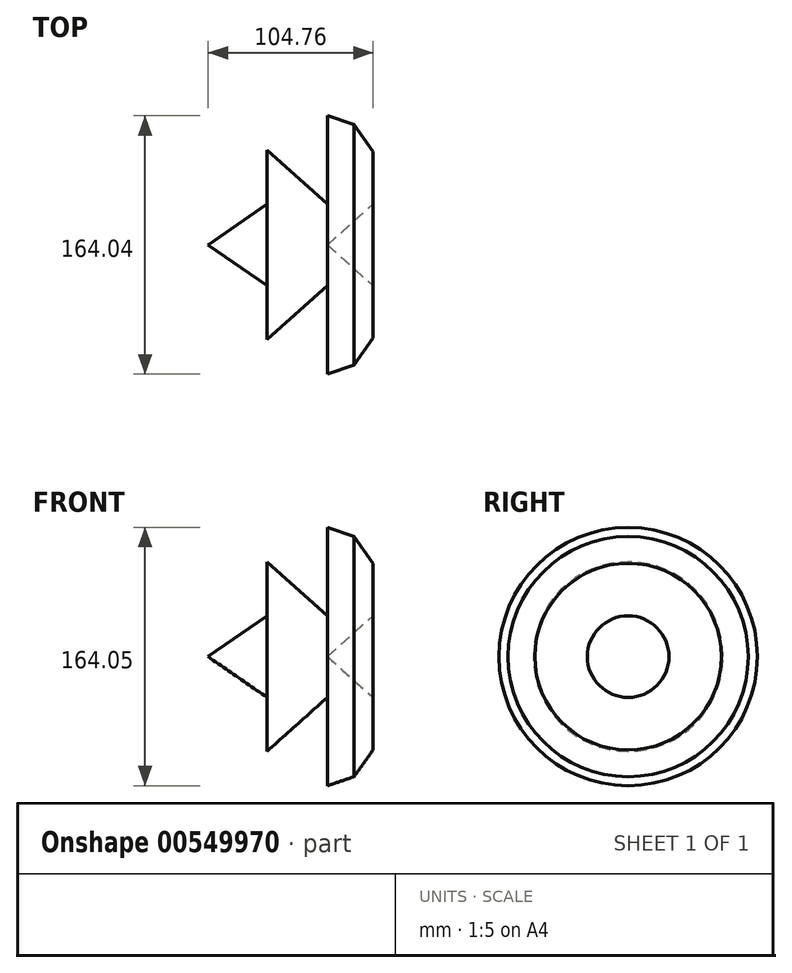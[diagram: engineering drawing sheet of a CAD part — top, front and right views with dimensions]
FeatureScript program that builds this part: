
annotation { "Feature Type Name" : "Feature", "Feature Type Description" : "" }
export const myFeature = defineFeature(function(context is Context, id is Id, definition is map)
    precondition{}
    {
        {
            var Q0;
            Q0=qCreatedBy(makeId("Front.planeOp"),FACE);
            var sketch = newSketch(context, id + "F0", { "sketchPlane" : qUnion([Q0])});
            skLineSegment(sketch, "E0", {"start": v(0, 25.9) * mm, "end": v(-75.7, 25.9) * mm});
            skLineSegment(sketch, "E1", {"start": v(0, 25.9) * mm, "end": v(29.07, 0) * mm});
            skLineSegment(sketch, "E2", {"start": v(29.07, 0) * mm, "end": v(29.07, -33.39) * mm});
            skLineSegment(sketch, "E3", {"start": v(-75.7, 25.9) * mm, "end": v(-38.28, 0) * mm});
            skLineSegment(sketch, "E4", {"start": v(-38.28, 0) * mm, "end": v(-38.28, -34.25) * mm});
            skLineSegment(sketch, "E5", {"start": v(-38.28, -34.25) * mm, "end": v(0, 0) * mm});
            skLineSegment(sketch, "E6", {"start": v(0, 0) * mm, "end": v(0, -56.12) * mm});
            skLineSegment(sketch, "E7", {"start": v(0, -56.12) * mm, "end": v(16.98, -50.37) * mm});
            skLineSegment(sketch, "E8", {"start": v(29.07, -33.39) * mm, "end": v(16.98, -50.37) * mm});
            skSolve(sketch);
        }
        {
            var Q0;
            Q0=makeQuery(id+"F0.imprint","IMPRINT",FACE,{"disambiguationData":[TD([[makeQuery(id+"F0.imprint","IMPRINT",EDGE,{"derivedFrom":sQuery(id+"F0.wireOp",EDGE,"E0")}),1.0]])]});
            var Q1;
            Q1=sQuery(id+"F0.wireOp",EDGE,"E0");
            revolve(context, id + "F1", {"entities" : qUnion([Q0]), "axis" : qUnion([Q1]), "revolveType" : RevolveType.FULL});
        }
    });
